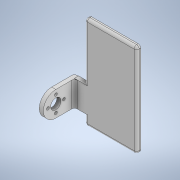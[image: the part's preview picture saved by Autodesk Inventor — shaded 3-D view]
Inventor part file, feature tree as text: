
AUTODESK INVENTOR PART (.ipt)
format: ipt  version: 2020 (Build 240168000, 168)  size: 166,912 bytes
history: native  units: in
note: dims shown in document units (in); Inventor stores cm internally (conversion verified against a paired STEP export)
features: extrude x4, sketch x4, fillet x1
ambient origin geometry x8: Origin, YZ Plane, XZ Plane, XY Plane, X Axis, Y Axis, Z Axis, Center Point
bodies: Solid1 (feature_tree)
feature tree (9):
  extrude  "Extrusion1"  Depth=1.2in
  extrude  "Extrusion3"  Depth=0.1406in
  extrude  "Extrusion4"  Depth=0.1406in
  extrude  "Extrusion5"  Depth=0.2in TaperAngle=0.0deg
  fillet  "Fillet1"  Radius=1.1in
  sketch  "Sketch1"  dims[d0=1.2in d1=0.77in]
  sketch  "Sketch5"  dims[d2=0.1406in d3=0.1406in]
  sketch  "Sketch6"  dims[d4=0.1406in d5=0.1406in]
  sketch  "Sketch7"  dims[d6=0.5in d7=0.2in d8=0.0in d17=1.1in d18=1.2in d19=0.2in d20=0.0in d21=0.2in d22=0.5in d23=0.0in d24=2.5in d25=4.0in d26=0.5in d27=0.2in d28=0.0in d29=0.125in]
